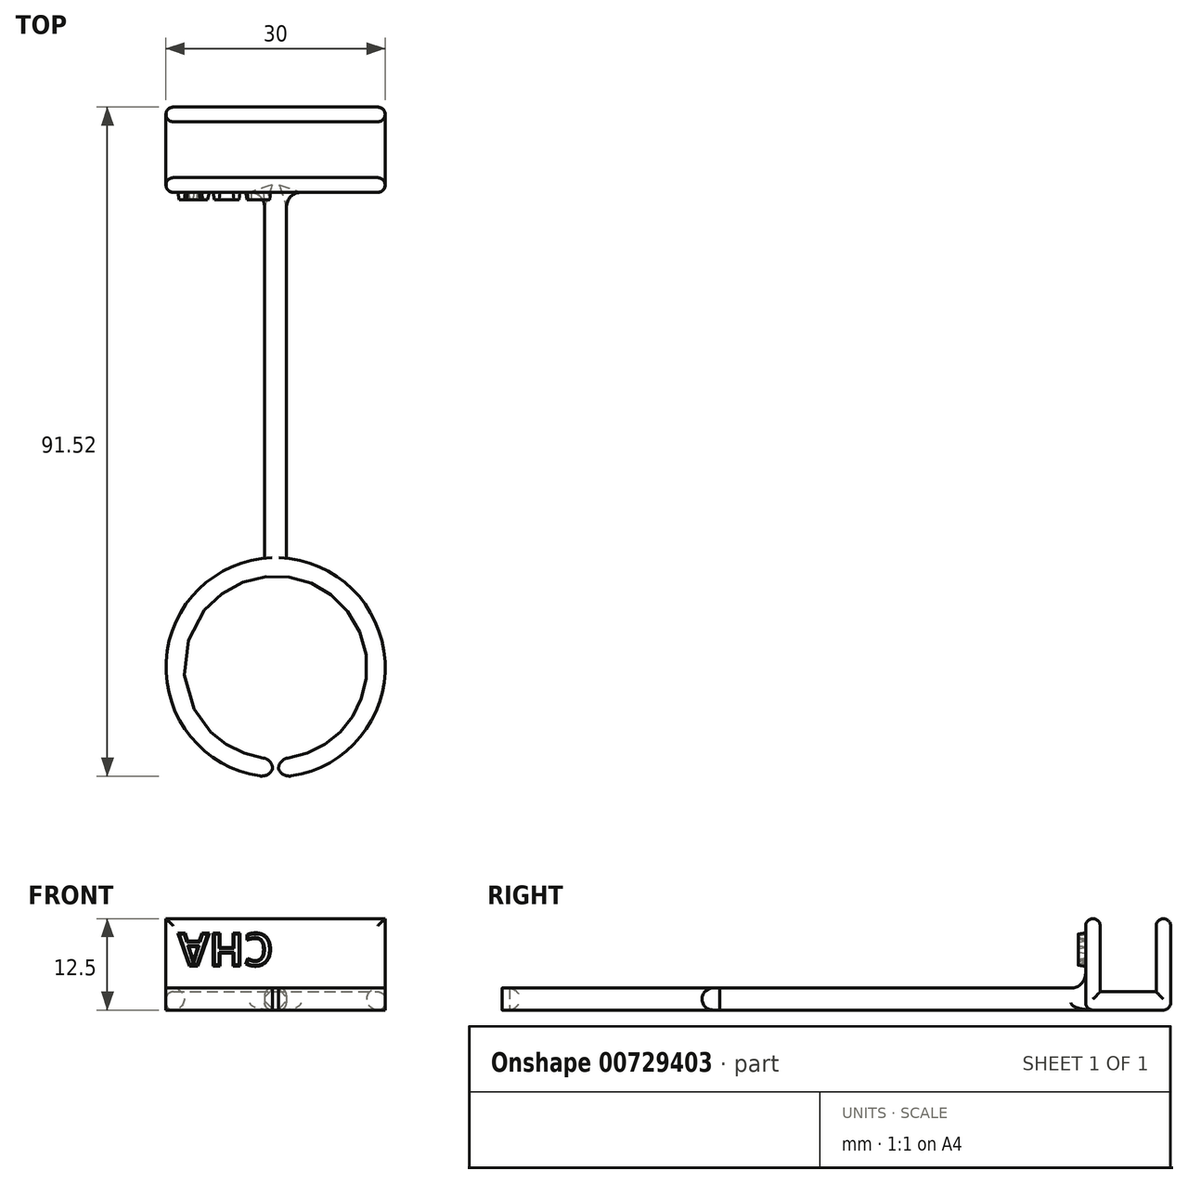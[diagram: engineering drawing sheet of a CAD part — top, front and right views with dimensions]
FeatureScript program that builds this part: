
annotation { "Feature Type Name" : "Feature", "Feature Type Description" : "" }
export const myFeature = defineFeature(function(context is Context, id is Id, definition is map)
    precondition{}
    {
        {
            var Q0;
            Q0=qCreatedBy(makeId("Right.planeOp"),FACE);
            var sketch = newSketch(context, id + "F0", { "sketchPlane" : qUnion([Q0])});
            skLineSegment(sketch, "E0.bottom", {"start": v(20, 0) * mm, "end": v(31.65, 0) * mm});
            skLineSegment(sketch, "E0.top", {"start": v(20, 12.5) * mm, "end": v(31.65, 12.5) * mm});
            skLineSegment(sketch, "E0.left", {"start": v(20, 0) * mm, "end": v(20, 12.5) * mm});
            skLineSegment(sketch, "E0.right", {"start": v(31.65, 0) * mm, "end": v(31.65, 12.5) * mm});
            skLineSegment(sketch, "E1.bottom", {"start": v(22, 0) * mm, "end": v(29.65, 0) * mm});
            skLineSegment(sketch, "E1.top", {"start": v(22, 10) * mm, "end": v(29.65, 10) * mm});
            skLineSegment(sketch, "E1.left", {"start": v(22, 0) * mm, "end": v(22, 10) * mm});
            skLineSegment(sketch, "E1.right", {"start": v(29.65, 0) * mm, "end": v(29.65, 10) * mm});
            skLineSegment(sketch, "E2.bottom", {"start": v(20, 12.5) * mm, "end": v(-30, 12.5) * mm});
            skLineSegment(sketch, "E2.top", {"start": v(20, 9.5) * mm, "end": v(-30, 9.5) * mm});
            skLineSegment(sketch, "E2.left", {"start": v(20, 12.5) * mm, "end": v(20, 9.5) * mm});
            skLineSegment(sketch, "E2.right", {"start": v(-30, 12.5) * mm, "end": v(-30, 9.5) * mm});
            skSolve(sketch);
        }
        {
            var Q0;
            Q0=makeQuery(id+"F0.imprint","IMPRINT",FACE,{"disambiguationData":[TD([[makeQuery(id+"F0.imprint","IMPRINT",EDGE,{"derivedFrom":sQuery(id+"F0.wireOp",EDGE,"E0.top")}),-1.0]])]});
            extrude(context, id + "F1", {"entities" : qUnion([Q0]), "endBound" : BoundingType.SYMMETRIC, "depth" : 30 * mm, "offsetDistance" : 25 * mm, "hasSecondDirection" : true, "secondDirectionOppositeDirection" : true, "secondDirectionDepth" : 25 * mm});
        }
        {
            var Q0;
            Q0=makeQuery(id+"F0.imprint","IMPRINT",FACE,{"disambiguationData":[TD([[makeQuery(id+"F0.imprint","IMPRINT",EDGE,{"derivedFrom":sQuery(id+"F0.wireOp",EDGE,"E2.bottom")}),1.0]])]});
            extrude(context, id + "F2", {"entities" : qUnion([Q0]), "operationType" : NewBodyOperationType.ADD, "endBound" : BoundingType.SYMMETRIC, "depth" : 3 * mm, "offsetDistance" : 25 * mm, "hasSecondDirection" : true, "secondDirectionOppositeDirection" : true, "secondDirectionDepth" : 5 * mm});
        }
        {
            var Q0;
            Q0=makeQuery(id+"F2.opExtrude","SWEPT_FACE",FACE,{"disambiguationData":[OSD([sQuery(id+"F0.wireOp",EDGE,"E2.right")])]});
            var sketch = newSketch(context, id + "F3", { "sketchPlane" : qUnion([Q0])});
            skLineSegment(sketch, "E3", {"start": v(-1.5, 11) * mm, "end": v(1.5, 11) * mm, "construction": true});
            skLineSegment(sketch, "E4", {"start": v(0, 12.5) * mm, "end": v(0, 9.5) * mm, "construction": true});
            skLineSegment(sketch, "E5", {"start": v(-1.5, 11) * mm, "end": v(1.5, 11) * mm});
            skSolve(sketch);
        }
        {
            var Q0;
            Q0=sQuery(id+"F3.wireOp",EDGE,"E5");
            extrude(context, id + "F4", {"bodyType" : ToolBodyType.SURFACE, "surfaceEntities" : qUnion([Q0]), "depth" : 5 * mm, "offsetDistance" : 25 * mm});
        }
        {
            var Q0;
            Q0=makeQuery(id+"F4.opExtrude","SWEPT_FACE",FACE,{"disambiguationData":[OSD([sQuery(id+"F3.wireOp",EDGE,"E5")])]});
            var sketch = newSketch(context, id + "F5", { "sketchPlane" : qUnion([Q0])});
            skCircle(sketch, "E6", {"center": v(0, 45) * mm, "radius": 15 * mm});
            skPoint(sketch, "E6.centerSnap0", {"position": v(0, 30) * mm});
            skCircle(sketch, "E7", {"center": v(0, 45) * mm, "radius": 12.5 * mm});
            skLineSegment(sketch, "E8", {"start": v(0, 45) * mm, "end": v(0, 65.3) * mm});
            skSolve(sketch);
        }
        {
            var Q0;
            Q0=makeQuery(id+"F4.opExtrude","SWEPT_BODY",BODY,{"disambiguationData":[OSD([sQuery(id+"F3.wireOp",EDGE,"E5")])]});
            deleteBodies(context, id + "F6", {"entities" : qUnion([Q0])});
        }
        {
            var Q0;
            Q0 = qSketchRegion(id + "F5", true);
            var Q1;
            Q1=makeQuery(id+"F2.opExtrude","SWEPT_FACE",FACE,{"disambiguationData":[OSD([sQuery(id+"F0.wireOp",EDGE,"E2.top")])]});
            var Q2;
            Q2=makeQuery(id+"F2.boolean.opBoolean","MERGE",FACE,{"derivedFrom":[makeQuery(id+"F1.opExtrude","SWEPT_FACE",FACE,{"disambiguationData":[OSD([sQuery(id+"F0.wireOp",EDGE,"E0.top")])]}),makeQuery(id+"F2.opExtrude","SWEPT_FACE",FACE,{"disambiguationData":[OSD([sQuery(id+"F0.wireOp",EDGE,"E2.bottom")])]})]});
            extrude(context, id + "F7", {"entities" : qUnion([Q0]), "operationType" : NewBodyOperationType.ADD, "endBound" : BoundingType.UP_TO_SURFACE, "depth" : 25 * mm, "endBoundEntityFace" : qUnion([Q1]), "offsetDistance" : 25 * mm, "hasSecondDirection" : true, "secondDirectionBound" : SecondDirectionBoundingType.UP_TO_SURFACE, "secondDirectionOppositeDirection" : true, "secondDirectionDepth" : 25 * mm, "secondDirectionBoundEntityFace" : qUnion([Q2])});
        }
        {
            var Q0;
            {var subQ0=sQuery(id+"F3.wireOp",EDGE,"E5");Q0=makeQuery(id+"F3.imprint","IMPRINT",FACE,{"disambiguationData":[TD([[makeQuery(id+"F3.imprint","IMPRINT",EDGE,{"derivedFrom":subQ0}),-1.0]])]});}
            var Q1;
            {var subQ0=sQuery(id+"F3.wireOp",EDGE,"E5");Q1=makeQuery(id+"F3.imprint","IMPRINT",FACE,{"disambiguationData":[TD([[makeQuery(id+"F3.imprint","IMPRINT",EDGE,{"derivedFrom":subQ0}),1.0]])]});}
            var Q2;
            Q2=makeQuery(id+"F7.opExtrude","SWEPT_FACE",FACE,{"disambiguationData":[OSD([sQuery(id+"F5.wireOp",EDGE,"E7")])]});
            var Q3;
            Q3=makeQuery(id+"F7.opExtrude","SWEPT_BODY",BODY,{"disambiguationData":[OSD([sQuery(id+"F5.wireOp",EDGE,"E6")])]});
            extrude(context, id + "F8", {"entities" : qUnion([Q0, Q1]), "operationType" : NewBodyOperationType.ADD, "endBound" : BoundingType.UP_TO_SURFACE, "depth" : 1.5 * mm, "endBoundEntityFace" : qUnion([Q2]), "endBoundEntityBody" : qUnion([Q3]), "offsetDistance" : 25 * mm});
        }
        {
            var Q0;
            Q0=sQuery(id+"F5.wireOp",EDGE,"E8");
            extrude(context, id + "F9", {"bodyType" : ToolBodyType.SURFACE, "surfaceEntities" : qUnion([Q0]), "endBound" : BoundingType.SYMMETRIC, "depth" : 5 * mm, "offsetDistance" : 25 * mm});
        }
        {
            var Q0;
            Q0=makeQuery(id+"F9.opExtrude","SWEPT_FACE",FACE,{"disambiguationData":[OSD([sQuery(id+"F5.wireOp",EDGE,"E8")])]});
            extrude(context, id + "F10", {"entities" : qUnion([Q0]), "operationType" : NewBodyOperationType.REMOVE, "endBound" : BoundingType.SYMMETRIC, "depth" : 0.8 * mm, "offsetDistance" : 25 * mm});
        }
        {
            var Q0;
            Q0=makeQuery(id+"F8.opExtrude","TWEAK_EDGE",EDGE,{"derivedFrom":[makeQuery(id+"F3.imprint","IMPRINT",EDGE,{"derivedFrom":makeQuery(id+"F2.opExtrude","SWEPT_EDGE",EDGE,{"disambiguationData":[OSD([sQuery(id+"F0.wireOp",EDGE,"E2.bottom"),sQuery(id+"F0.wireOp",EDGE,"E2.right")])]})}),makeQuery(id+"F7.opExtrude","SWEPT_FACE",FACE,{"disambiguationData":[OSD([sQuery(id+"F5.wireOp",EDGE,"E7")])]})]});
            var Q1;
            Q1=makeQuery(id+"F8.opExtrude","TWEAK_EDGE",EDGE,{"derivedFrom":[makeQuery(id+"F3.imprint","IMPRINT",EDGE,{"derivedFrom":makeQuery(id+"F2.opExtrude","SWEPT_EDGE",EDGE,{"disambiguationData":[OSD([sQuery(id+"F0.wireOp",EDGE,"E2.top"),sQuery(id+"F0.wireOp",EDGE,"E2.right")])]})}),makeQuery(id+"F7.opExtrude","SWEPT_FACE",FACE,{"disambiguationData":[OSD([sQuery(id+"F5.wireOp",EDGE,"E7")])]})]});
            var Q2;
            Q2=makeQuery(id+"F7.opExtrude","SWEPT_FACE",FACE,{"disambiguationData":[OSD([sQuery(id+"F5.wireOp",EDGE,"E7")])]});
            fillet(context, id + "F11", {"entities" : qUnion([Q0, Q1, Q2]), "radius" : 1.5 * mm, "tangentPropagation" : true, "allowEdgeOverflow" : false});
        }
        {
            var Q0;
            {var subQ0=sQuery(id+"F5.wireOp",EDGE,"E6");var subQ1=makeQuery(id+"F5.imprint","INTERSECT",VERTEX,{"derivedFrom":[subQ0,sQuery(id+"F5.wireOp",EDGE,"E8")]});var subQ4=makeQuery(id+"F5.imprint","INTERSECT",VERTEX,{"derivedFrom":[makeQuery(id+"F4.opExtrude","CAP_EDGE",EDGE,{"disambiguationData":[OSD([sQuery(id+"F3.wireOp",EDGE,"E5")])],"isStart":true}),subQ0]});Q0=makeQuery(id+"F7.opExtrude","TWEAK_EDGE",EDGE,{"derivedFrom":[makeQuery(id+"F2.boolean.opBoolean","MERGE",FACE,{"derivedFrom":[makeQuery(id+"F1.opExtrude","SWEPT_FACE",FACE,{"disambiguationData":[OSD([sQuery(id+"F0.wireOp",EDGE,"E0.top")])]}),makeQuery(id+"F2.opExtrude","SWEPT_FACE",FACE,{"disambiguationData":[OSD([sQuery(id+"F0.wireOp",EDGE,"E2.bottom")])]})]}),makeQuery(id+"F5.imprint","IMPRINT",EDGE,{"disambiguationData":[TD([[subQ4,1.0]])],"derivedFrom":subQ0}),makeQuery(id+"F5.imprint","IMPRINT",EDGE,{"disambiguationData":[TD([[subQ4,-1.0]])],"derivedFrom":subQ0}),makeQuery(id+"F5.imprint","IMPRINT",EDGE,{"disambiguationData":[TD([[subQ1,1.0]])],"derivedFrom":subQ0}),makeQuery(id+"F5.imprint","IMPRINT",EDGE,{"disambiguationData":[TD([[subQ1,-1.0]])],"derivedFrom":subQ0})]});}
            var Q1;
            {var subQ0=sQuery(id+"F5.wireOp",EDGE,"E6");var subQ1=makeQuery(id+"F5.imprint","INTERSECT",VERTEX,{"derivedFrom":[subQ0,sQuery(id+"F5.wireOp",EDGE,"E8")]});var subQ4=makeQuery(id+"F5.imprint","INTERSECT",VERTEX,{"derivedFrom":[makeQuery(id+"F4.opExtrude","CAP_EDGE",EDGE,{"disambiguationData":[OSD([sQuery(id+"F3.wireOp",EDGE,"E5")])],"isStart":true}),subQ0]});Q1=makeQuery(id+"F7.opExtrude","TWEAK_EDGE",EDGE,{"derivedFrom":[makeQuery(id+"F2.opExtrude","SWEPT_FACE",FACE,{"disambiguationData":[OSD([sQuery(id+"F0.wireOp",EDGE,"E2.top")])]}),makeQuery(id+"F5.imprint","IMPRINT",EDGE,{"disambiguationData":[TD([[subQ4,1.0]])],"derivedFrom":subQ0}),makeQuery(id+"F5.imprint","IMPRINT",EDGE,{"disambiguationData":[TD([[subQ4,-1.0]])],"derivedFrom":subQ0}),makeQuery(id+"F5.imprint","IMPRINT",EDGE,{"disambiguationData":[TD([[subQ1,1.0]])],"derivedFrom":subQ0}),makeQuery(id+"F5.imprint","IMPRINT",EDGE,{"disambiguationData":[TD([[subQ1,-1.0]])],"derivedFrom":subQ0})]});}
            var Q2;
            Q2=makeQuery(id+"F10.boolean.opBoolean","INTERSECT",EDGE,{"derivedFrom":[makeQuery(id+"F7.opExtrude","SWEPT_FACE",FACE,{"disambiguationData":[OSD([sQuery(id+"F5.wireOp",EDGE,"E6")])]}),makeQuery(id+"F10.opExtrude","CAP_FACE",FACE,{"disambiguationData":[OSD([sQuery(id+"F5.wireOp",EDGE,"E8")])],"isStart":true})]});
            var Q3;
            Q3=makeQuery(id+"F10.boolean.opBoolean","INTERSECT",EDGE,{"derivedFrom":[makeQuery(id+"F7.opExtrude","SWEPT_FACE",FACE,{"disambiguationData":[OSD([sQuery(id+"F5.wireOp",EDGE,"E6")])]}),makeQuery(id+"F10.opExtrude","CAP_FACE",FACE,{"disambiguationData":[OSD([sQuery(id+"F5.wireOp",EDGE,"E8")])],"isStart":false})]});
            fillet(context, id + "F12", {"entities" : qUnion([Q0, Q1, Q2, Q3]), "radius" : 1.6 * mm, "tangentPropagation" : true, "allowEdgeOverflow" : false});
        }
        {
            var Q0;
            {var subQ0=sQuery(id+"F0.wireOp",EDGE,"E2.right");var subQ1=sQuery(id+"F0.wireOp",EDGE,"E2.bottom");Q0=makeQuery(id+"F8.boolean.opBoolean","MERGE",EDGE,{"derivedFrom":[makeQuery(id+"F2.opExtrude","CAP_EDGE",EDGE,{"disambiguationData":[OSD([subQ1])],"isStart":false}),makeQuery(id+"F8.opExtrude","SWEPT_EDGE",EDGE,{"disambiguationData":[OSD([subQ1,subQ0]),TDD([makeQuery(id+"F3.imprint","INTERSECT",VERTEX,{"derivedFrom":[makeQuery(id+"F2.opExtrude","SWEPT_EDGE",EDGE,{"disambiguationData":[OSD([subQ1,subQ0])]}),makeQuery(id+"F2.opExtrude","CAP_EDGE",EDGE,{"disambiguationData":[OSD([subQ0])],"isStart":false})]})])]})]});}
            var Q1;
            {var subQ0=sQuery(id+"F0.wireOp",EDGE,"E2.right");var subQ1=sQuery(id+"F0.wireOp",EDGE,"E2.top");Q1=makeQuery(id+"F8.boolean.opBoolean","MERGE",EDGE,{"derivedFrom":[makeQuery(id+"F2.opExtrude","CAP_EDGE",EDGE,{"disambiguationData":[OSD([subQ1])],"isStart":false}),makeQuery(id+"F8.opExtrude","SWEPT_EDGE",EDGE,{"disambiguationData":[OSD([subQ1,subQ0]),TDD([makeQuery(id+"F3.imprint","INTERSECT",VERTEX,{"derivedFrom":[makeQuery(id+"F2.opExtrude","SWEPT_EDGE",EDGE,{"disambiguationData":[OSD([subQ1,subQ0])]}),makeQuery(id+"F2.opExtrude","CAP_EDGE",EDGE,{"disambiguationData":[OSD([subQ0])],"isStart":false})]})])]})]});}
            var Q2;
            {var subQ0=sQuery(id+"F0.wireOp",EDGE,"E2.right");var subQ1=sQuery(id+"F0.wireOp",EDGE,"E2.bottom");Q2=makeQuery(id+"F8.boolean.opBoolean","MERGE",EDGE,{"derivedFrom":[makeQuery(id+"F2.opExtrude","CAP_EDGE",EDGE,{"disambiguationData":[OSD([subQ1])],"isStart":true}),makeQuery(id+"F8.opExtrude","SWEPT_EDGE",EDGE,{"disambiguationData":[OSD([subQ1,subQ0]),TDD([makeQuery(id+"F3.imprint","INTERSECT",VERTEX,{"derivedFrom":[makeQuery(id+"F2.opExtrude","SWEPT_EDGE",EDGE,{"disambiguationData":[OSD([subQ1,subQ0])]}),makeQuery(id+"F2.opExtrude","CAP_EDGE",EDGE,{"disambiguationData":[OSD([subQ0])],"isStart":true})]})])]})]});}
            var Q3;
            {var subQ0=sQuery(id+"F0.wireOp",EDGE,"E2.right");var subQ1=sQuery(id+"F0.wireOp",EDGE,"E2.top");Q3=makeQuery(id+"F8.boolean.opBoolean","MERGE",EDGE,{"derivedFrom":[makeQuery(id+"F2.opExtrude","CAP_EDGE",EDGE,{"disambiguationData":[OSD([subQ1])],"isStart":true}),makeQuery(id+"F8.opExtrude","SWEPT_EDGE",EDGE,{"disambiguationData":[OSD([subQ1,subQ0]),TDD([makeQuery(id+"F3.imprint","INTERSECT",VERTEX,{"derivedFrom":[makeQuery(id+"F2.opExtrude","SWEPT_EDGE",EDGE,{"disambiguationData":[OSD([subQ1,subQ0])]}),makeQuery(id+"F2.opExtrude","CAP_EDGE",EDGE,{"disambiguationData":[OSD([subQ0])],"isStart":true})]})])]})]});}
            var Q4;
            Q4=makeQuery(id+"F1.opExtrude","SWEPT_EDGE",EDGE,{"disambiguationData":[OSD([sQuery(id+"F0.wireOp",EDGE,"E0.bottom"),sQuery(id+"F0.wireOp",EDGE,"E1.bottom"),sQuery(id+"F0.wireOp",EDGE,"E1.left")])]});
            var Q5;
            Q5=makeQuery(id+"F1.opExtrude","SWEPT_EDGE",EDGE,{"disambiguationData":[OSD([sQuery(id+"F0.wireOp",EDGE,"E0.bottom"),sQuery(id+"F0.wireOp",EDGE,"E1.bottom"),sQuery(id+"F0.wireOp",EDGE,"E1.right")])]});
            var Q6;
            Q6=makeQuery(id+"F1.opExtrude","SWEPT_EDGE",EDGE,{"disambiguationData":[OSD([sQuery(id+"F0.wireOp",EDGE,"E0.bottom"),sQuery(id+"F0.wireOp",EDGE,"E0.left")])]});
            var Q7;
            Q7=makeQuery(id+"F1.opExtrude","SWEPT_EDGE",EDGE,{"disambiguationData":[OSD([sQuery(id+"F0.wireOp",EDGE,"E0.bottom"),sQuery(id+"F0.wireOp",EDGE,"E0.right")])]});
            var Q8;
            {var subQ0=sQuery(id+"F0.wireOp",EDGE,"E2.bottom");var subQ1=sQuery(id+"F0.wireOp",EDGE,"E0.top");var subQ2=sQuery(id+"F0.wireOp",EDGE,"E2.left");Q8=makeQuery(id+"F2.boolean.opBoolean","SPLIT",EDGE,{"disambiguationData":[TD([makeQuery(id+"F2.opExtrude","CAP_FACE",FACE,{"disambiguationData":[OSD([subQ0,sQuery(id+"F0.wireOp",EDGE,"E2.top"),subQ2,sQuery(id+"F0.wireOp",EDGE,"E2.right")])],"isStart":false})])],"derivedFrom":makeQuery(id+"F1.opExtrude","SWEPT_EDGE",EDGE,{"disambiguationData":[OSD([subQ1,subQ0,subQ2])]})});}
            var Q9;
            {var subQ0=sQuery(id+"F0.wireOp",EDGE,"E2.left");var subQ2=sQuery(id+"F0.wireOp",EDGE,"E2.bottom");var subQ3=sQuery(id+"F0.wireOp",EDGE,"E0.top");Q9=makeQuery(id+"F2.boolean.opBoolean","SPLIT",EDGE,{"disambiguationData":[TD([makeQuery(id+"F2.opExtrude","CAP_FACE",FACE,{"disambiguationData":[OSD([subQ2,sQuery(id+"F0.wireOp",EDGE,"E2.top"),subQ0,sQuery(id+"F0.wireOp",EDGE,"E2.right")])],"isStart":true})])],"derivedFrom":makeQuery(id+"F1.opExtrude","SWEPT_EDGE",EDGE,{"disambiguationData":[OSD([subQ3,subQ2,subQ0])]})});}
            var Q10;
            Q10=makeQuery(id+"F1.opExtrude","CAP_EDGE",EDGE,{"disambiguationData":[OSD([sQuery(id+"F0.wireOp",EDGE,"E0.left"),sQuery(id+"F0.wireOp",EDGE,"E2.left")])],"isStart":false});
            var Q11;
            Q11=makeQuery(id+"F1.opExtrude","CAP_EDGE",EDGE,{"disambiguationData":[OSD([sQuery(id+"F0.wireOp",EDGE,"E1.left")])],"isStart":false});
            var Q12;
            Q12=makeQuery(id+"F1.opExtrude","CAP_EDGE",EDGE,{"disambiguationData":[OSD([sQuery(id+"F0.wireOp",EDGE,"E1.top")])],"isStart":false});
            var Q13;
            Q13=makeQuery(id+"F1.opExtrude","CAP_EDGE",EDGE,{"disambiguationData":[OSD([sQuery(id+"F0.wireOp",EDGE,"E1.right")])],"isStart":false});
            var Q14;
            Q14=makeQuery(id+"F1.opExtrude","CAP_EDGE",EDGE,{"disambiguationData":[OSD([sQuery(id+"F0.wireOp",EDGE,"E0.right")])],"isStart":false});
            var Q15;
            Q15=makeQuery(id+"F1.opExtrude","CAP_EDGE",EDGE,{"disambiguationData":[OSD([sQuery(id+"F0.wireOp",EDGE,"E0.top")])],"isStart":false});
            var Q16;
            Q16=makeQuery(id+"F1.opExtrude","CAP_EDGE",EDGE,{"disambiguationData":[OSD([sQuery(id+"F0.wireOp",EDGE,"E0.top")])],"isStart":true});
            var Q17;
            Q17=makeQuery(id+"F1.opExtrude","CAP_EDGE",EDGE,{"disambiguationData":[OSD([sQuery(id+"F0.wireOp",EDGE,"E0.left"),sQuery(id+"F0.wireOp",EDGE,"E2.left")])],"isStart":true});
            var Q18;
            Q18=makeQuery(id+"F1.opExtrude","CAP_EDGE",EDGE,{"disambiguationData":[OSD([sQuery(id+"F0.wireOp",EDGE,"E1.left")])],"isStart":true});
            var Q19;
            Q19=makeQuery(id+"F1.opExtrude","CAP_EDGE",EDGE,{"disambiguationData":[OSD([sQuery(id+"F0.wireOp",EDGE,"E1.top")])],"isStart":true});
            var Q20;
            Q20=makeQuery(id+"F1.opExtrude","CAP_EDGE",EDGE,{"disambiguationData":[OSD([sQuery(id+"F0.wireOp",EDGE,"E1.right")])],"isStart":true});
            var Q21;
            Q21=makeQuery(id+"F1.opExtrude","SWEPT_EDGE",EDGE,{"disambiguationData":[OSD([sQuery(id+"F0.wireOp",EDGE,"E0.top"),sQuery(id+"F0.wireOp",EDGE,"E0.right")])]});
            var Q22;
            Q22=makeQuery(id+"F1.opExtrude","CAP_EDGE",EDGE,{"disambiguationData":[OSD([sQuery(id+"F0.wireOp",EDGE,"E0.right")])],"isStart":true});
            fillet(context, id + "F13", {"entities" : qUnion([Q0, Q1, Q2, Q3, Q4, Q5, Q6, Q7, Q8, Q9, Q10, Q11, Q12, Q13, Q14, Q15, Q16, Q17, Q18, Q19, Q20, Q21, Q22]), "radius" : 1 * mm, "allowEdgeOverflow" : false});
        }
        {
            var Q0;
            {var subQ0=sQuery(id+"F0.wireOp",EDGE,"E2.right");var subQ1=sQuery(id+"F0.wireOp",EDGE,"E2.top");Q0=makeQuery(id+"F13.opFillet","BLEND_EDGE",EDGE,{"blendedFrom":[makeQuery(id+"F8.boolean.opBoolean","MERGE",EDGE,{"derivedFrom":[makeQuery(id+"F2.opExtrude","CAP_EDGE",EDGE,{"disambiguationData":[OSD([subQ1])],"isStart":true}),makeQuery(id+"F8.opExtrude","SWEPT_EDGE",EDGE,{"disambiguationData":[OSD([subQ1,subQ0]),TDD([makeQuery(id+"F3.imprint","INTERSECT",VERTEX,{"derivedFrom":[makeQuery(id+"F2.opExtrude","SWEPT_EDGE",EDGE,{"disambiguationData":[OSD([subQ1,subQ0])]}),makeQuery(id+"F2.opExtrude","CAP_EDGE",EDGE,{"disambiguationData":[OSD([subQ0])],"isStart":true})]})])]})]}),makeQuery(id+"F1.opExtrude","SWEPT_FACE",FACE,{"disambiguationData":[OSD([sQuery(id+"F0.wireOp",EDGE,"E0.left"),sQuery(id+"F0.wireOp",EDGE,"E2.left")])]})],"blendedInto":[makeQuery(id+"F1.opExtrude","SWEPT_FACE",FACE,{"disambiguationData":[OSD([sQuery(id+"F0.wireOp",EDGE,"E0.left"),sQuery(id+"F0.wireOp",EDGE,"E2.left")])]})]});}
            fillet(context, id + "F14", {"entities" : qUnion([Q0]), "radius" : 2 * mm, "tangentPropagation" : true, "allowEdgeOverflow" : false});
        }
        {
            var Q0;
            Q0=makeQuery(id+"F1.opExtrude","SWEPT_FACE",FACE,{"disambiguationData":[OSD([sQuery(id+"F0.wireOp",EDGE,"E0.left"),sQuery(id+"F0.wireOp",EDGE,"E2.left")])]});
            var sketch = newSketch(context, id + "F15", { "sketchPlane" : qUnion([Q0])});
            skText(sketch, "E9", { "text": "CHA", "fontName": "OpenSans-Bold.ttf"});
            const initialGuessF15  = {"E9": [0.00032, 0.002, 1, 0, 0.0045]};
            skSetInitialGuess(sketch, initialGuessF15);
            skSolve(sketch);
        }
        {
            var Q0;
            Q0 = qSketchRegion(id + "F15", true);
            extrude(context, id + "F16", {"entities" : qUnion([Q0]), "operationType" : NewBodyOperationType.ADD, "depth" : 1 * mm, "offsetDistance" : 25 * mm, "hasDraft" : true, "draftAngle" : 8 * degree, "draftPullDirection" : true});
        }
        {
            var Q0;
            Q0=makeQuery(id+"F1.opExtrude","SWEPT_BODY",BODY,{"disambiguationData":[OSD([sQuery(id+"F0.wireOp",EDGE,"E0.bottom"),sQuery(id+"F0.wireOp",EDGE,"E0.top"),sQuery(id+"F0.wireOp",EDGE,"E0.left"),sQuery(id+"F0.wireOp",EDGE,"E0.right"),sQuery(id+"F0.wireOp",EDGE,"E1.top"),sQuery(id+"F0.wireOp",EDGE,"E1.left"),sQuery(id+"F0.wireOp",EDGE,"E1.right"),sQuery(id+"F0.wireOp",EDGE,"E2.left")])]});
            var Q1;
            {var subQ0=sQuery(id+"F0.wireOp",EDGE,"E2.right");var subQ1=sQuery(id+"F0.wireOp",EDGE,"E2.bottom");Q1=makeQuery(id+"F13.opFillet","BLEND_EDGE",EDGE,{"blendedFrom":[makeQuery(id+"F8.boolean.opBoolean","MERGE",EDGE,{"derivedFrom":[makeQuery(id+"F2.opExtrude","CAP_EDGE",EDGE,{"disambiguationData":[OSD([subQ1])],"isStart":true}),makeQuery(id+"F8.opExtrude","SWEPT_EDGE",EDGE,{"disambiguationData":[OSD([subQ1,subQ0]),TDD([makeQuery(id+"F3.imprint","INTERSECT",VERTEX,{"derivedFrom":[makeQuery(id+"F2.opExtrude","SWEPT_EDGE",EDGE,{"disambiguationData":[OSD([subQ1,subQ0])]}),makeQuery(id+"F2.opExtrude","CAP_EDGE",EDGE,{"disambiguationData":[OSD([subQ0])],"isStart":true})]})])]})]}),makeQuery(id+"F8.boolean.opBoolean","MERGE",FACE,{"derivedFrom":[makeQuery(id+"F2.boolean.opBoolean","MERGE",FACE,{"derivedFrom":[makeQuery(id+"F1.opExtrude","SWEPT_FACE",FACE,{"disambiguationData":[OSD([sQuery(id+"F0.wireOp",EDGE,"E0.top")])]}),makeQuery(id+"F2.opExtrude","SWEPT_FACE",FACE,{"disambiguationData":[OSD([subQ1])]})]}),makeQuery(id+"F8.opExtrude","SWEPT_FACE",FACE,{"disambiguationData":[OSD([subQ1,subQ0])]})]})],"blendedInto":[makeQuery(id+"F8.boolean.opBoolean","MERGE",FACE,{"derivedFrom":[makeQuery(id+"F2.boolean.opBoolean","MERGE",FACE,{"derivedFrom":[makeQuery(id+"F1.opExtrude","SWEPT_FACE",FACE,{"disambiguationData":[OSD([sQuery(id+"F0.wireOp",EDGE,"E0.top")])]}),makeQuery(id+"F2.opExtrude","SWEPT_FACE",FACE,{"disambiguationData":[OSD([subQ1])]})]}),makeQuery(id+"F8.opExtrude","SWEPT_FACE",FACE,{"disambiguationData":[OSD([subQ1,subQ0])]})]})]});}
            transform(context, id + "F17", {"entities" : qUnion([Q0]), "transformType" : TransformType.ROTATION, "transformAxis" : qUnion([Q1]), "angle" : 180 * degree, "makeCopy" : false});
        }
    });
